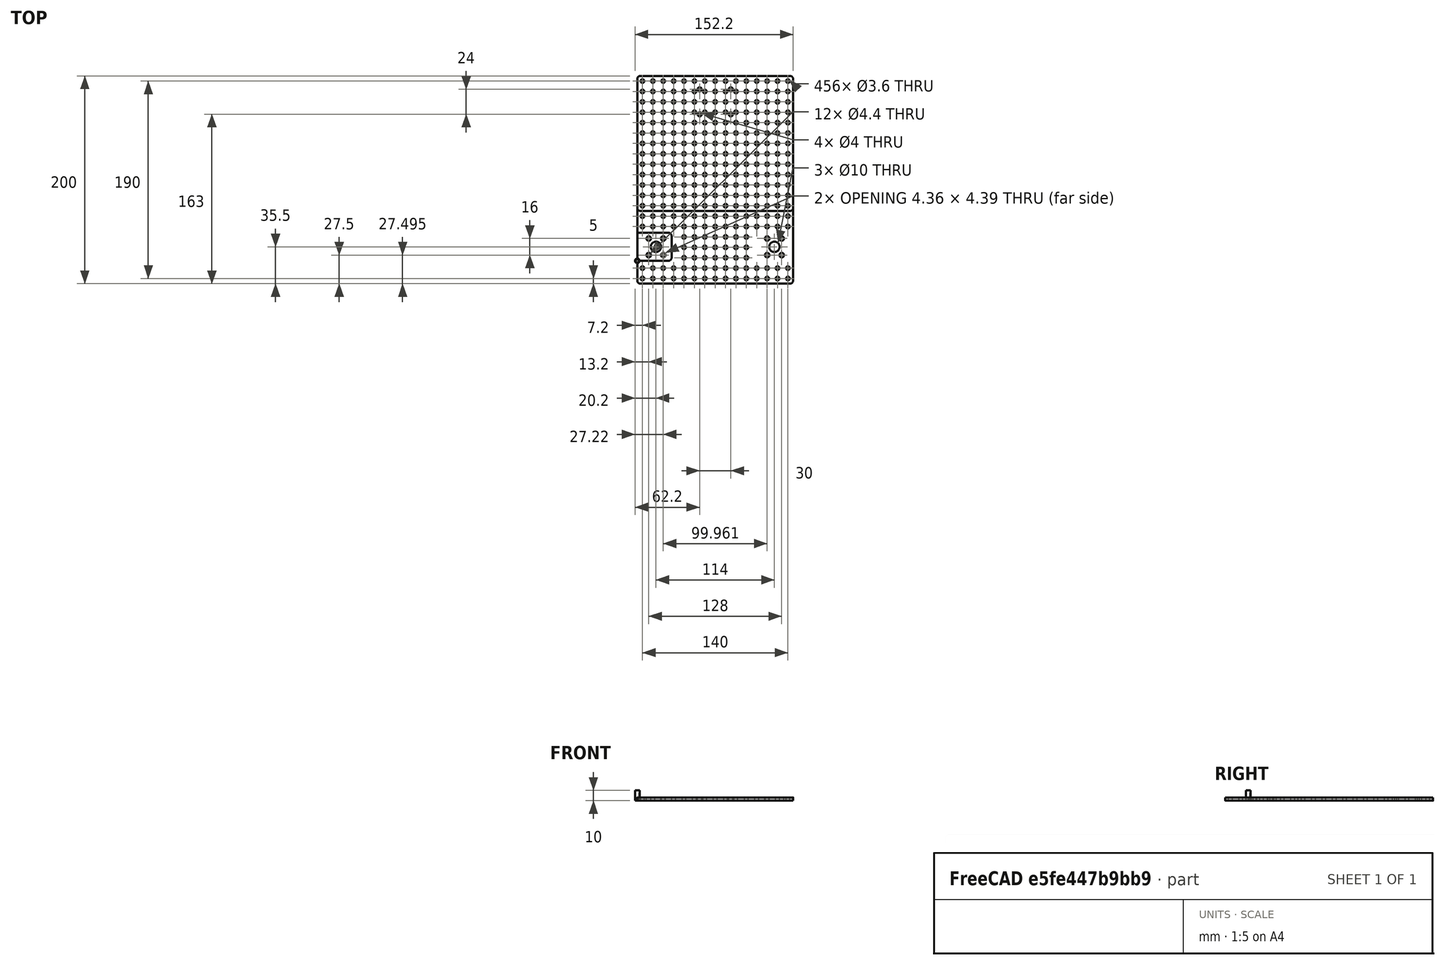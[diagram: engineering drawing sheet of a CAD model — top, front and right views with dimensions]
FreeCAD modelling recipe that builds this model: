
FCSTD DOCUMENT  (FreeCAD 0.19R23578 (Git))
Label: vehicle_plate4wheels
License: All rights reserved
LicenseURL: http://en.wikipedia.org/wiki/All_rights_reserved
objects: Part::Box×5, Part::Cylinder×4, Part::MultiFuse×4, Part::Cut×4, Part::Fillet×3, Part::FeaturePython×3, Part::Mirroring×2, PartDesign::FeatureBase×1, PartDesign::Body×1, Part::Refine×1
note: 25 computed .brp shape members not serialized (recipe doc carries the construction recipe); baked Part::Feature solids carry a one-line shape summary decoded from their .brp

FEATURE [Part::Box] Box  label="plate"
  AttacherType = Attacher::AttachEngine3D
  Height = 3
  Length = 150
  Width = 200
FEATURE [Part::Box] Box001  label="motor holder box"
  AttacherType = Attacher::AttachEngine3D
  Height = 3
  Length = 33
  Width = 27
FEATURE [Part::Fillet] Fillet  label="motor holder box fillet"
  Base = -> Box001
  Edges = 2 edges r=3: [Edge5,Edge7]
FEATURE [Part::Cylinder] Cylinder  label="bolt hole"
  Angle = 360
  AttacherType = Attacher::AttachEngine3D
  Height = 10
  Radius = 2.2
FEATURE [Part::FeaturePython] Array  label="bolt hole array"  # Draft array (typed FeaturePython)
  Angle = 360
  ArrayType = 0
  Axis = (0,0,1)
  Base = -> Cylinder
  Center = (0,0,0)
  Count = 4
  ExpandArray = false
  Fuse = false
  IntervalAxis = (0,0,0)
  IntervalX = (14,0,0)
  IntervalY = (0,16,0)
  IntervalZ = (0,0,100)
  NumberCircles = 3
  NumberPolar = 5
  NumberX = 2
  NumberY = 2
  NumberZ = 1
  Placement = pos=(11,5.5,0) rot=(0,0,1;0rad)
  PlacementList = 4 placements: [(0,0,0),(0,16,0),(14,0,0),(14,16,0)]
  RadialDistance = 50
  ScaleList = (4) [(1,1,1),(1,1,1),(1,1,1),(1,1,1)]
  Symmetry = 1
  TangentialDistance = 25
  expr: .Placement.Base.y = (<<motor holder box>>.Width - .IntervalY.y) / 2
FEATURE [Part::Cylinder] Cylinder001  label="motor holder central hole"
  Angle = 360
  AttacherType = Attacher::AttachEngine3D
  Height = 10
  Placement = pos=(18,13.5,0) rot=(0,0,1;0rad)
  Radius = 5
  expr: .Placement.Base.y = <<motor holder box>>.Width / 2
  expr: .Placement.Base.x = <<bolt hole array>>.Placement.Base.x + <<bolt hole array>>.IntervalX.x / 2
FEATURE [Part::MultiFuse] Fusion  label="hole extract"
  Shapes = -> [Array,Cylinder001]
FEATURE [Part::Cut] Cut  label="motor holder cut"
  Base = -> Fillet
  Tool = -> Fusion
FEATURE [PartDesign::FeatureBase] Clone
  BaseFeature = -> Fusion
FEATURE [PartDesign::Body] Body  label="motor holder hole extract clone"
  BaseFeature = -> Fusion
  Group = -> [Clone]
  Origin = -> Origin
  Tip = -> Clone
FEATURE [Part::Mirroring] Part__Mirroring  label="motor holder hole extract clone (Mirror #1)"
  Base = (75,0,0)
  Normal = (1,0,0)
  Source = -> Body
  expr: .Base.x = <<plate>>.Length / 2
FEATURE [Part::Cylinder] Cylinder002  label="m3 hole"
  Angle = 360
  AttacherType = Attacher::AttachEngine3D
  Height = 10
  Radius = 1.8
FEATURE [Part::FeaturePython] Array001  label="m3 hole array"  # Draft array (typed FeaturePython)
  Angle = 360
  ArrayType = 0
  Axis = (0,0,1)
  Base = -> Cylinder002
  Center = (0,0,0)
  Count = 300
  ExpandArray = false
  Fuse = false
  IntervalAxis = (0,0,0)
  IntervalX = (10,0,0)
  IntervalY = (0,10,0)
  IntervalZ = (0,0,100)
  NumberCircles = 3
  NumberPolar = 5
  NumberX = 15
  NumberY = 20
  NumberZ = 1
  Placement = pos=(5,5,0) rot=(0,0,1;0rad)
  PlacementList = 300 placements: [(0,0,0),(0,10,0),(0,20,0),(0,30,0),(0,40,0),(0,50,0),(0,60,0),(0,70,0),(0,80,0),(0,90,0),(0,100,0),(0,110,0),(0,120,0),(0,130,0),(0,140,0),(0,150,0),(0,160,0),(0,170,0),(0,180,0),(0,190,0),(10,0,0),(10,10,0),(10,20,0),(10,30,0),(10,40,0),(10,50,0),(10,60,0),(10,70,0),(10,80,0),(10,90,0),(10,100,0),(10,110,0),(10,120,0),(10,130,0),(10,140,0),(10,150,0),(10,160,0),(10,170,0),(10,180,0),(10,190,0),+260 more]
  RadialDistance = 50
  Symmetry = 1
  TangentialDistance = 25
  expr: .Placement.Base.x = .IntervalX.x / 2
  expr: .Placement.Base.y = .IntervalY.y / 2
  expr: NumberX = <<plate>>.Length / 10
  expr: NumberY = <<plate>>.Width / 10
FEATURE [Part::Box] Box002  label="motor plate patch"
  AttacherType = Attacher::AttachEngine3D
  Height = 3
  Length = 43
  Placement = pos=(0,-3,0) rot=(0,0,1;0rad)
  Width = 33
  expr: Length = <<motor holder box>>.Length + 10mm
  expr: Width = <<motor holder box>>.Width + 6mm
  expr: Height = <<motor holder box>>.Height
  expr: .Placement.Base.y = <<motor holder box>>.Placement.Base.y - (Width - <<motor holder box>>.Width) / 2
FEATURE [Part::Mirroring] Part__Mirroring001  label="motor plate patch (Mirror #2)"
  Base = (75,0,0)
  Normal = (1,0,0)
  Source = -> Box002
  expr: .Base.x = <<motor holder hole extract clone (Mirror #1)>>.Base.x
FEATURE [Part::Cylinder] Cylinder003  label="m4 hole"
  Angle = 360
  AttacherType = Attacher::AttachEngine3D
  Height = 10
  Radius = 2
FEATURE [Part::FeaturePython] Array002  label="caster hole array"  # Draft array (typed FeaturePython)
  Angle = 360
  ArrayType = 0
  Axis = (0,0,1)
  Base = -> Cylinder003
  Center = (0,0,0)
  Count = 4
  ExpandArray = false
  Fuse = false
  IntervalAxis = (0,0,0)
  IntervalX = (30,0,0)
  IntervalY = (0,24,0)
  IntervalZ = (0,0,100)
  NumberCircles = 3
  NumberPolar = 5
  NumberX = 2
  NumberY = 2
  NumberZ = 1
  Placement = pos=(60,141,0) rot=(0,0,1;0rad)
  PlacementList = 4 placements: [(0,0,0),(0,24,0),(30,0,0),(30,24,0)]
  RadialDistance = 50
  ScaleList = (4) [(1,1,1),(1,1,1),(1,1,1),(1,1,1)]
  Symmetry = 1
  TangentialDistance = 25
  expr: .Placement.Base.x = (<<plate>>.Length - .IntervalX.x) / 2
  expr: .Placement.Base.y = <<plate>>.Width - .IntervalY.y * 2 - 11mm
FEATURE [Part::MultiFuse] Fusion003  label="plate hole fusion"
  Shapes = -> [Part__Mirroring,Body,Array002]
FEATURE [Part::Box] Box003  label="caster patch"
  AttacherType = Attacher::AttachEngine3D
  Height = 3
  Length = 46
  Placement = pos=(52,136,0) rot=(0,0,1;0rad)
  Width = 34
  expr: Length = <<caster hole array>>.IntervalX.x + 16mm
  expr: Width = <<caster hole array>>.IntervalY.y + 10mm
  expr: Height = <<plate>>.Height
  expr: .Placement.Base.x = <<caster hole array>>.Placement.Base.x - (Length - <<caster hole array>>.IntervalX.x) / 2
  expr: .Placement.Base.y = <<caster hole array>>.Placement.Base.y - (Width - <<caster hole array>>.IntervalY.y) / 2
FEATURE [Part::MultiFuse] Fusion001  label="patch fusion"
  Shapes = -> [Part__Mirroring001,Box002,Box003]
FEATURE [Part::Fillet] Fillet001  label="plate fillet"
  Base = -> Box
  Edges = 4 edges r=3: [Edge1,Edge3,Edge5,Edge7]
FEATURE [Part::Cut] Cut001  label="plate cut"
  Base = -> Fillet001
  Placement = pos=(0,-22,0) rot=(0,0,1;0rad)
  Tool = -> Array001
FEATURE [Part::MultiFuse] Fusion002  label="plate fusion"
  Shapes = -> [Cut001,Fusion001]
FEATURE [Part::Cut] Cut002  label="holed plate cut"
  Base = -> Fusion002
  Tool = -> Fusion003
FEATURE [Part::Refine] Cut002001  label="holed plate cut001"
  Source = -> Cut002
FEATURE [Part::Box] Box004  label="top plate"
  AttacherType = Attacher::AttachEngine3D
  Height = 3
  Length = 150
  Width = 130
FEATURE [Part::Fillet] Fillet002  label="top plate fillet"
  Base = -> Box004
  Edges = 4 edges r=3: [Edge1,Edge3,Edge5,Edge7]
FEATURE [Part::Cut] Cut002002  label="top plate cut"
  Base = -> Fillet002
  Placement = pos=(0,48,0) rot=(0,0,1;0rad)
  Tool = -> Array001
  expr: .Placement.Base.y = <<plate>>.Width - <<top plate>>.Width + <<plate cut>>.Placement.Base.y
